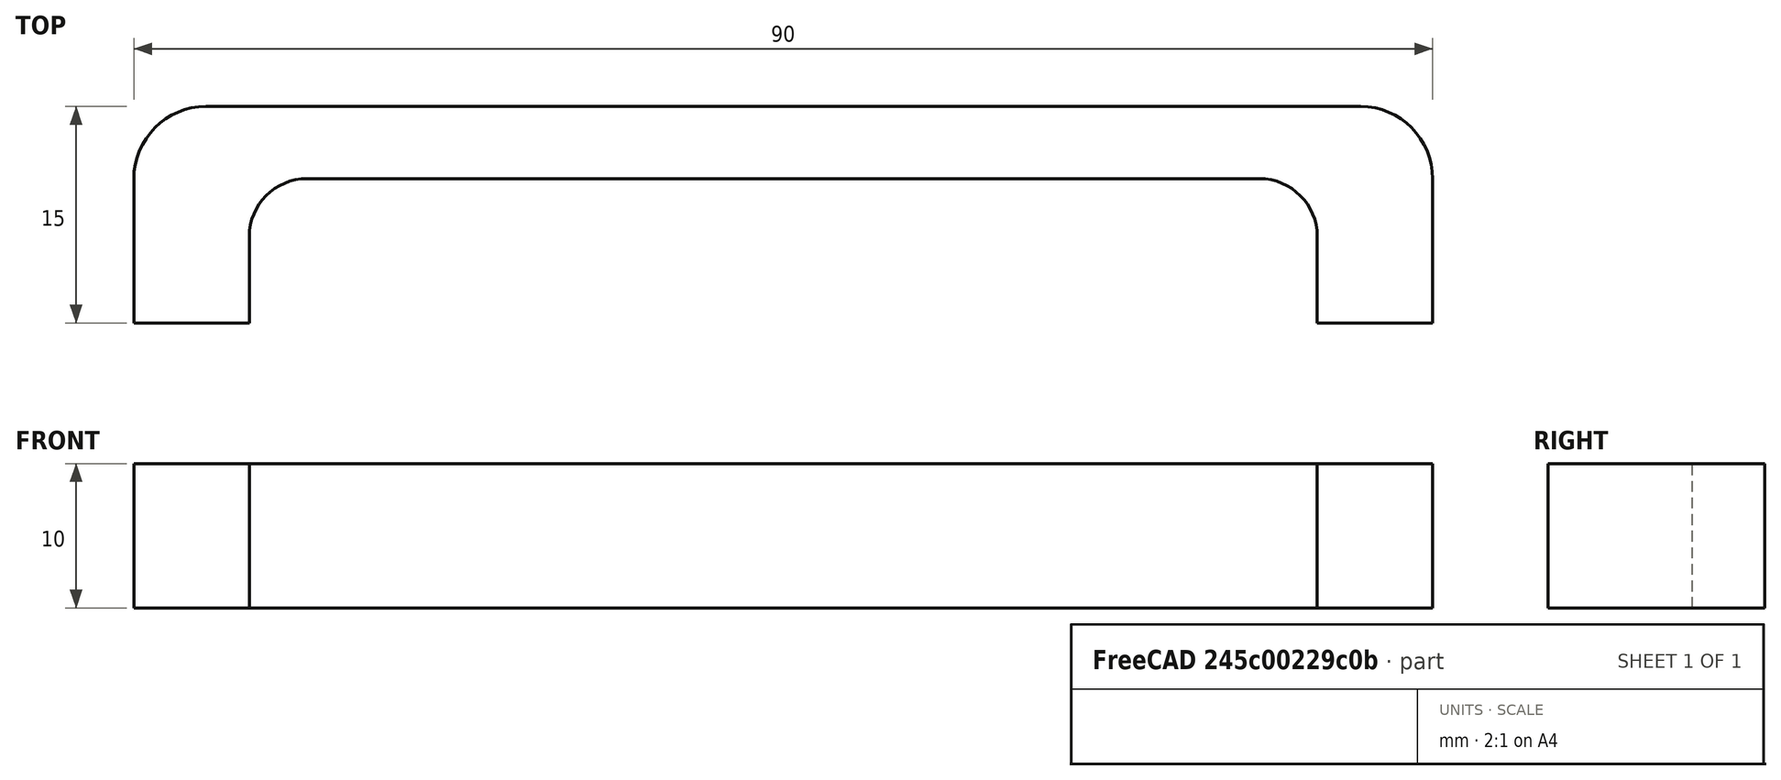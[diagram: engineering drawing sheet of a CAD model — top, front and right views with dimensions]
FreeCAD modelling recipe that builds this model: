
FCSTD DOCUMENT  (FreeCAD 0.20R)
Label: zip_tie_cutout
License: All rights reserved
LicenseURL: http://en.wikipedia.org/wiki/All_rights_reserved
objects: Sketcher::SketchObject×1, PartDesign::Pad×1, PartDesign::Body×1
note: 4 computed .brp shape members not serialized (recipe doc carries the construction recipe); baked Part::Feature solids carry a one-line shape summary decoded from their .brp

FEATURE [Sketcher::SketchObject] Sketch
  FullyConstrained = true
  MapMode = 5
  Support = -> [XY_Plane]
  sketch-geometry (12):
    g0: LineSegment StartX=-45 StartY=1e-16 StartZ=0 EndX=-45 EndY=10 EndZ=0
    g1: LineSegment StartX=-40 StartY=15 StartZ=0 EndX=40 EndY=15 EndZ=0
    g2: LineSegment StartX=45 StartY=10 StartZ=0 EndX=45 EndY=0 EndZ=0
    g3: LineSegment StartX=45 StartY=0 StartZ=0 EndX=37 EndY=-1e-16 EndZ=0
    g4: LineSegment StartX=37 StartY=-1e-16 StartZ=0 EndX=37 EndY=6 EndZ=0
    g5: LineSegment StartX=33 StartY=10 StartZ=0 EndX=-33 EndY=10 EndZ=0
    g6: LineSegment StartX=-37 StartY=6 StartZ=0 EndX=-37 EndY=0 EndZ=0
    g7: LineSegment StartX=-37 StartY=1e-16 StartZ=0 EndX=-45 EndY=1e-16 EndZ=0
    g8: ArcOfCircle CenterX=-33 CenterY=6 CenterZ=0 NormalX=0 NormalY=0 NormalZ=1 AngleXU=0 Radius=4 StartAngle=1.5708 EndAngle=3.14159
    g9: ArcOfCircle CenterX=33 CenterY=6 CenterZ=0 NormalX=0 NormalY=0 NormalZ=1 AngleXU=0 Radius=4 StartAngle=0 EndAngle=1.5708
    g10: ArcOfCircle CenterX=-40 CenterY=10 CenterZ=0 NormalX=0 NormalY=0 NormalZ=1 AngleXU=0 Radius=5 StartAngle=1.5708 EndAngle=3.14159
    g11: ArcOfCircle CenterX=40 CenterY=10 CenterZ=0 NormalX=0 NormalY=0 NormalZ=1 AngleXU=0 Radius=5 StartAngle=0 EndAngle=1.5708
  constraints (31):
    c: Vertical(g0)
    c: Horizontal(g1)
    c: Vertical(g2)
    c: Coincident(g2,g3)
    c: Coincident(g3,g4)
    c: Vertical(g4)
    c: Horizontal(g5)
    c: Coincident(g6,g7)
    c: Coincident(g7,g0)
    c: Parallel(g6,g0)
    c: Parallel(g7,g1)
    c: Parallel(g3,g1)
    c: Equal(g3,g7)
    c: Equal(g4,g6)
    c: Tangent(g6,g8) = -1.5708
    c: Tangent(g5,g8) = -1.5708
    c: Tangent(g5,g9) = -1.5708
    c: Tangent(g4,g9) = -1.5708
    c: Tangent(g1,g10) = 1.5708
    c: Tangent(g0,g10) = 1.5708
    c: Tangent(g1,g11) = 1.5708
    c: Tangent(g2,g11) = 1.5708
    c: Equal(g11,g10)
    c: Equal(g8,g9)
    c: DistanceY(g6,g6) = 6
    c: Radius(g9) = 4
    c: Radius(g10) = 5
    c: DistanceX(g7,g7) = 8
    c: DistanceX(g1,g1) = 80
    c: DistanceY(g0,g0) = 10
    c: Symmetric(g2,g0,g-1)
FEATURE [PartDesign::Pad] Pad
  Direction = (0,0,1)
  Length = 10
  Length2 = 10
  Profile = -> Sketch
  ReferenceAxis = -> Sketch [N_Axis]
  Type = 0
FEATURE [PartDesign::Body] Body
  Group = -> [Sketch,Pad]
  Origin = -> Origin
  Tip = -> Pad
